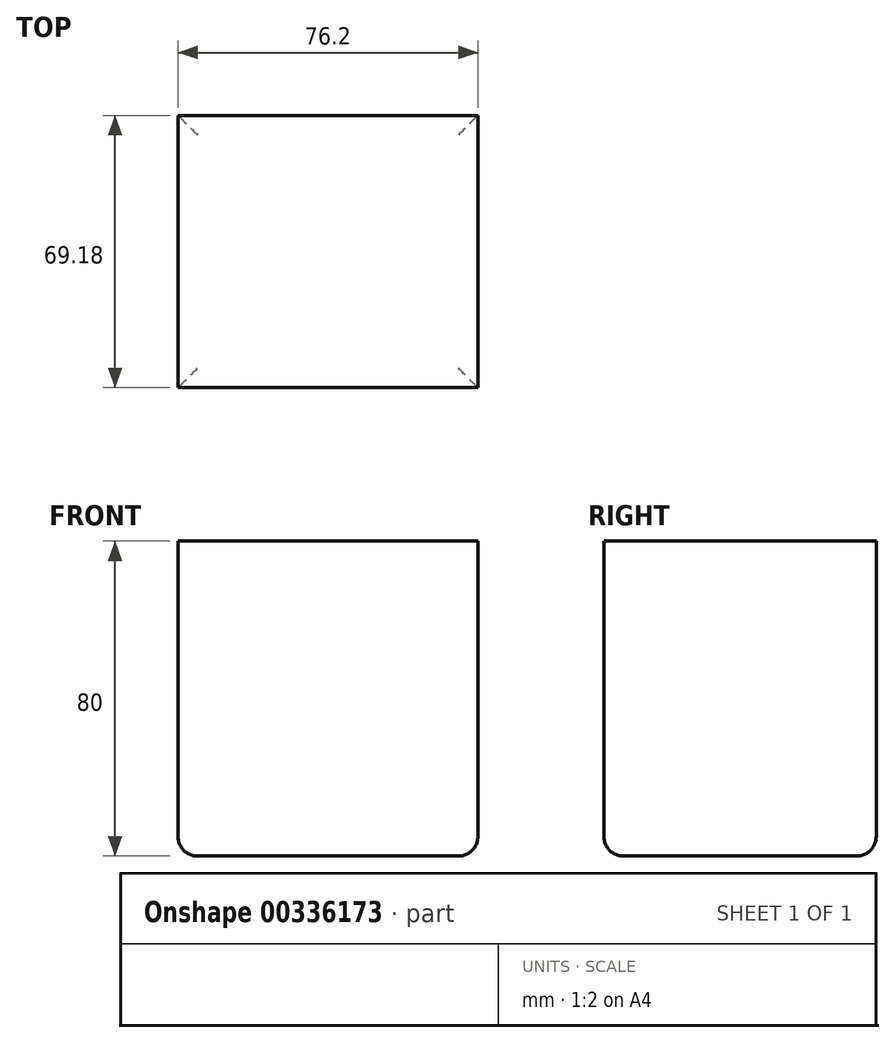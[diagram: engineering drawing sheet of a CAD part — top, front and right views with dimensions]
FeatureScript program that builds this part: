
annotation { "Feature Type Name" : "Feature", "Feature Type Description" : "" }
export const myFeature = defineFeature(function(context is Context, id is Id, definition is map)
    precondition{}
    {
        {
            var Q0;
            Q0=qCreatedBy(makeId("Top.planeOp"),FACE);
            var sketch = newSketch(context, id + "F0", { "sketchPlane" : qUnion([Q0])});
            skLineSegment(sketch, "E0.bottom", {"start": v(38.1, -34.6) * mm, "end": v(-38.1, -34.6) * mm});
            skLineSegment(sketch, "E0.top", {"start": v(38.1, 34.6) * mm, "end": v(-38.1, 34.6) * mm});
            skLineSegment(sketch, "E0.left", {"start": v(38.1, -34.6) * mm, "end": v(38.1, 34.6) * mm});
            skLineSegment(sketch, "E0.right", {"start": v(-38.1, -34.6) * mm, "end": v(-38.1, 34.6) * mm});
            skPoint(sketch, "E0.middle", {"position": v(0, 0) * mm});
            skLineSegment(sketch, "E1.bottom", {"start": v(0, -5.64) * mm, "end": v(0, -5.64) * mm});
            skLineSegment(sketch, "E1.top", {"start": v(0, 74.83) * mm, "end": v(0, 74.83) * mm});
            skLineSegment(sketch, "E1.left", {"start": v(0, -5.64) * mm, "end": v(0, 74.83) * mm});
            skLineSegment(sketch, "E1.right", {"start": v(0, -5.64) * mm, "end": v(0, 74.83) * mm});
            skPoint(sketch, "E1.middle", {"position": v(0, 34.6) * mm});
            skPoint(sketch, "E1.cornerSnap0", {"position": v(0, 34.6) * mm});
            skSolve(sketch);
        }
        {
            var Q0;
            Q0=makeQuery(id+"F0.imprint","IMPRINT",FACE,{"disambiguationData":[TD([[makeQuery(id+"F0.imprint","IMPRINT",EDGE,{"derivedFrom":sQuery(id+"F0.wireOp",EDGE,"E0.bottom")}),-1.0]])]});
            extrude(context, id + "F1", {"entities" : qUnion([Q0]), "endBound" : BoundingType.SYMMETRIC, "depth" : 80 * mm});
        }
        {
            var Q0;
            Q0=makeQuery(id+"F1.opExtrude","CAP_FACE",FACE,{"disambiguationData":[OSD([sQuery(id+"F0.wireOp",EDGE,"E0.bottom"),sQuery(id+"F0.wireOp",EDGE,"E0.top"),sQuery(id+"F0.wireOp",EDGE,"E0.left"),sQuery(id+"F0.wireOp",EDGE,"E0.right")])],"isStart":true});
            fillet(context, id + "F2", {"entities" : qUnion([Q0]), "radius" : 5 * mm, "tangentPropagation" : true, "allowEdgeOverflow" : false});
        }
    });
